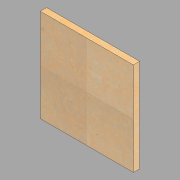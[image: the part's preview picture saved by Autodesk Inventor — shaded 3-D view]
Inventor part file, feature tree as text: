
AUTODESK INVENTOR PART (.ipt)
format: ipt  version: 2022.1 (Build 261234020, 234B)  size: 104,960 bytes
history: native  units: in
note: dims shown in document units (in); Inventor stores cm internally (conversion verified against a paired STEP export)
features: extrude x1, sketch x1
ambient origin geometry x8: Origin, YZ Plane, XZ Plane, XY Plane, X Axis, Y Axis, Z Axis, Center Point
bodies: Solid1 (feature_tree)
feature tree (2):
  extrude  "Extrusion1"  Depth=29.625in
  sketch  "Sketch1"  dims[d0=29.625in d1=29.625in d2=2.0in d3=0.0in]
